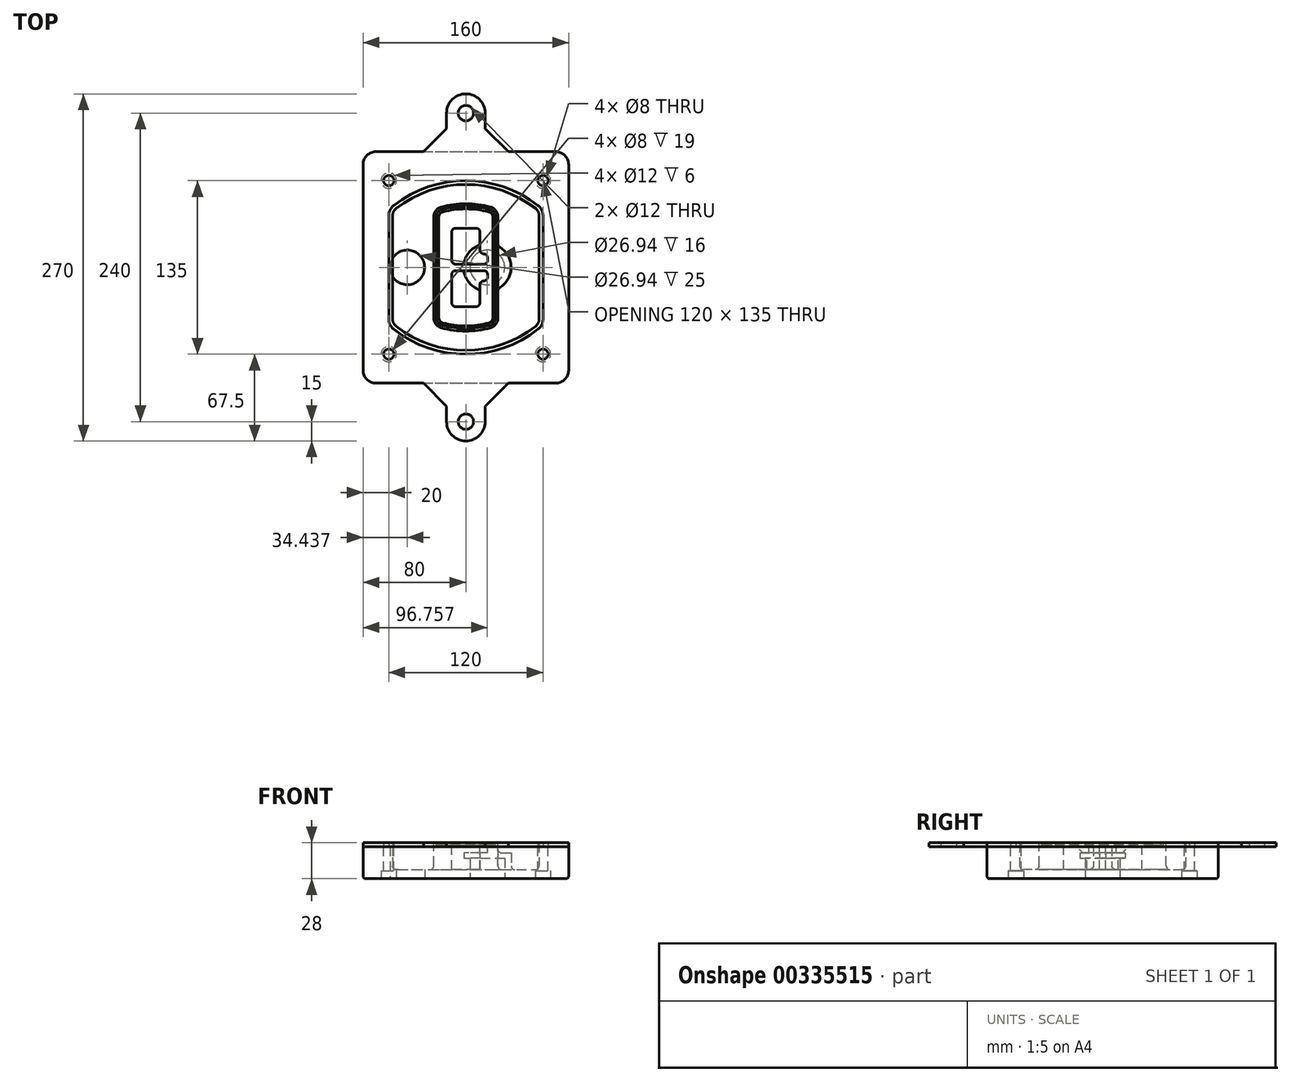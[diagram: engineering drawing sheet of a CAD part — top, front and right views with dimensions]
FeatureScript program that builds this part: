
annotation { "Feature Type Name" : "Feature", "Feature Type Description" : "" }
export const myFeature = defineFeature(function(context is Context, id is Id, definition is map)
    precondition{}
    {
        {
            var Q0;
            Q0=qCreatedBy(makeId("Top.planeOp"),FACE);
            var sketch = newSketch(context, id + "F0", { "sketchPlane" : qUnion([Q0])});
            skPoint(sketch, "E0.rect.middle", {"position": v(0, 0) * mm});
            skLineSegment(sketch, "E1.bottom", {"start": v(-70, -90) * mm, "end": v(70, -90) * mm});
            skLineSegment(sketch, "E1.top", {"start": v(-70, 90) * mm, "end": v(70, 90) * mm});
            skLineSegment(sketch, "E1.left", {"start": v(-80, -80) * mm, "end": v(-80, 80) * mm});
            skLineSegment(sketch, "E1.right", {"start": v(80, -80) * mm, "end": v(80, 80) * mm});
            skLineSegment(sketch, "E2", {"start": v(-80, 90) * mm, "end": v(80, -90) * mm, "construction": true});
            skLineSegment(sketch, "E3", {"start": v(80, 90) * mm, "end": v(-80, -90) * mm, "construction": true});
            skCircle(sketch, "E4", {"center": v(-60, 67.5) * mm, "radius": 4 * mm});
            skCircle(sketch, "E5", {"center": v(60, 67.5) * mm, "radius": 4 * mm});
            skCircle(sketch, "E6", {"center": v(60, -67.5) * mm, "radius": 4 * mm});
            skCircle(sketch, "E7", {"center": v(-60, -67.5) * mm, "radius": 4 * mm});
            skLineSegment(sketch, "E8", {"start": v(-60, 67.5) * mm, "end": v(60, 67.5) * mm, "construction": true});
            skLineSegment(sketch, "E9", {"start": v(60, 67.5) * mm, "end": v(60, -67.5) * mm, "construction": true});
            skLineSegment(sketch, "E10", {"start": v(60, -67.5) * mm, "end": v(-60, -67.5) * mm, "construction": true});
            skLineSegment(sketch, "E11", {"start": v(-60, -67.5) * mm, "end": v(-60, 67.5) * mm, "construction": true});
            skLineSegment(sketch, "E12", {"start": v(-60, 40.3) * mm, "end": v(-60, -40.3) * mm});
            skLineSegment(sketch, "E13", {"start": v(60, 40.3) * mm, "end": v(60, -40.3) * mm});
            skArc(sketch, "E14", {"start": v(56.15, 48.18) * mm, "mid": v(0, 67.5) * mm, "end": v(-56.15, 48.18) * mm});
            skArc(sketch, "E15", {"start": v(-56.15, -48.18) * mm, "mid": v(0, -67.5) * mm, "end": v(56.15, -48.18) * mm});
            skLineSegment(sketch, "E16", {"start": v(-60, 0) * mm, "end": v(60, 0) * mm, "construction": true});
            skPoint(sketch, "E17.visualSharp", {"position": v(-60, -45) * mm});
            skArc(sketch, "E17.filletArc", {"start": v(-60, -40.3) * mm, "mid": v(-58.99, -44.68) * mm, "end": v(-56.15, -48.18) * mm});
            skPoint(sketch, "E18.visualSharp", {"position": v(-60, 45) * mm});
            skArc(sketch, "E18.filletArc", {"start": v(-56.15, 48.18) * mm, "mid": v(-58.99, 44.68) * mm, "end": v(-60, 40.3) * mm});
            skPoint(sketch, "E19.visualSharp", {"position": v(60, 45) * mm});
            skArc(sketch, "E19.filletArc", {"start": v(60, 40.3) * mm, "mid": v(58.99, 44.68) * mm, "end": v(56.15, 48.18) * mm});
            skPoint(sketch, "E20.visualSharp", {"position": v(60, -45) * mm});
            skArc(sketch, "E20.filletArc", {"start": v(56.15, -48.18) * mm, "mid": v(58.99, -44.68) * mm, "end": v(60, -40.3) * mm});
            skPoint(sketch, "E21.visualSharp", {"position": v(-80, 90) * mm});
            skArc(sketch, "E21.filletArc", {"start": v(-70, 90) * mm, "mid": v(-77.07, 87.07) * mm, "end": v(-80, 80) * mm});
            skPoint(sketch, "E22.visualSharp", {"position": v(80, 90) * mm});
            skArc(sketch, "E22.filletArc", {"start": v(80, 80) * mm, "mid": v(77.07, 87.07) * mm, "end": v(70, 90) * mm});
            skPoint(sketch, "E23.visualSharp", {"position": v(80, -90) * mm});
            skArc(sketch, "E23.filletArc", {"start": v(70, -90) * mm, "mid": v(77.07, -87.07) * mm, "end": v(80, -80) * mm});
            skPoint(sketch, "E24.visualSharp", {"position": v(-80, -90) * mm});
            skArc(sketch, "E24.filletArc", {"start": v(-80, -80) * mm, "mid": v(-77.07, -87.07) * mm, "end": v(-70, -90) * mm});
            skArc(sketch, "E25.0", {"start": v(57, 40.3) * mm, "mid": v(56.3, 43.36) * mm, "end": v(54.3, 45.81) * mm});
            skLineSegment(sketch, "E25.1", {"start": v(57, 40.3) * mm, "end": v(57, -40.3) * mm});
            skArc(sketch, "E25.2", {"start": v(54.3, -45.81) * mm, "mid": v(56.3, -43.36) * mm, "end": v(57, -40.3) * mm});
            skArc(sketch, "E25.3", {"start": v(-54.3, -45.81) * mm, "mid": v(0, -64.5) * mm, "end": v(54.3, -45.81) * mm});
            skArc(sketch, "E25.4", {"start": v(-57, -40.3) * mm, "mid": v(-56.3, -43.36) * mm, "end": v(-54.3, -45.81) * mm});
            skArc(sketch, "E25.5", {"start": v(54.3, 45.81) * mm, "mid": v(0, 64.5) * mm, "end": v(-54.3, 45.81) * mm});
            skLineSegment(sketch, "E25.6", {"start": v(-57, 40.3) * mm, "end": v(-57, -40.3) * mm});
            skArc(sketch, "E25.7", {"start": v(-54.3, 45.81) * mm, "mid": v(-56.3, 43.36) * mm, "end": v(-57, 40.3) * mm});
            skArc(sketch, "E26.0", {"start": v(-58.62, 51.33) * mm, "mid": v(-62.58, 46.43) * mm, "end": v(-64, 40.3) * mm});
            skArc(sketch, "E26.1", {"start": v(58.62, 51.33) * mm, "mid": v(0, 71.5) * mm, "end": v(-58.62, 51.33) * mm});
            skArc(sketch, "E26.2", {"start": v(64, 40.3) * mm, "mid": v(62.58, 46.43) * mm, "end": v(58.62, 51.33) * mm});
            skLineSegment(sketch, "E26.3", {"start": v(64, 40.3) * mm, "end": v(64, -40.3) * mm});
            skArc(sketch, "E26.4", {"start": v(58.62, -51.33) * mm, "mid": v(62.58, -46.43) * mm, "end": v(64, -40.3) * mm});
            skLineSegment(sketch, "E26.5", {"start": v(-64, 40.3) * mm, "end": v(-64, -40.3) * mm});
            skArc(sketch, "E26.6", {"start": v(-58.62, -51.33) * mm, "mid": v(0, -71.5) * mm, "end": v(58.62, -51.33) * mm});
            skArc(sketch, "E26.7", {"start": v(-64, -40.3) * mm, "mid": v(-62.58, -46.43) * mm, "end": v(-58.62, -51.33) * mm});
            skSolve(sketch);
        }
        {
            var Q0;
            Q0=makeQuery(id+"F0.imprint","IMPRINT",FACE,{"disambiguationData":[TD([[makeQuery(id+"F0.imprint","IMPRINT",EDGE,{"derivedFrom":sQuery(id+"F0.wireOp",EDGE,"E1.bottom")}),1.0]])]});
            var Q1;
            Q1=makeQuery(id+"F0.imprint","IMPRINT",FACE,{"disambiguationData":[TD([[makeQuery(id+"F0.imprint","IMPRINT",EDGE,{"derivedFrom":sQuery(id+"F0.wireOp",EDGE,"E12")}),1.0]])]});
            var Q2;
            Q2=makeQuery(id+"F0.imprint","IMPRINT",FACE,{"disambiguationData":[TD([[makeQuery(id+"F0.imprint","IMPRINT",EDGE,{"derivedFrom":sQuery(id+"F0.wireOp",EDGE,"E25.0")}),1.0]])]});
            var Q3;
            Q3=makeQuery(id+"F0.imprint","IMPRINT",FACE,{"disambiguationData":[TD([[makeQuery(id+"F0.imprint","IMPRINT",EDGE,{"derivedFrom":sQuery(id+"F0.wireOp",EDGE,"E12")}),-1.0]])]});
            extrude(context, id + "F1", {"entities" : qUnion([Q0, Q1, Q2, Q3]), "oppositeDirection" : true, "depth" : 25 * mm});
        }
        {
            var Q0;
            Q0=makeQuery(id+"F0.imprint","IMPRINT",FACE,{"disambiguationData":[TD([[makeQuery(id+"F0.imprint","IMPRINT",EDGE,{"derivedFrom":sQuery(id+"F0.wireOp",EDGE,"E12")}),1.0]])]});
            extrude(context, id + "F2", {"entities" : qUnion([Q0]), "operationType" : NewBodyOperationType.ADD, "depth" : 3 * mm});
        }
        {
            var Q0;
            Q0=makeQuery(id+"F0.imprint","IMPRINT",FACE,{"disambiguationData":[TD([[makeQuery(id+"F0.imprint","IMPRINT",EDGE,{"derivedFrom":sQuery(id+"F0.wireOp",EDGE,"E25.0")}),1.0]])]});
            extrude(context, id + "F3", {"entities" : qUnion([Q0]), "operationType" : NewBodyOperationType.REMOVE, "oppositeDirection" : true, "depth" : 18 * mm});
        }
        {
            var Q0;
            Q0=makeQuery(id+"F2.opExtrude","CAP_FACE",FACE,{"disambiguationData":[OSD([sQuery(id+"F0.wireOp",EDGE,"E12"),sQuery(id+"F0.wireOp",EDGE,"E13"),sQuery(id+"F0.wireOp",EDGE,"E14"),sQuery(id+"F0.wireOp",EDGE,"E15"),sQuery(id+"F0.wireOp",EDGE,"E17.filletArc"),sQuery(id+"F0.wireOp",EDGE,"E18.filletArc"),sQuery(id+"F0.wireOp",EDGE,"E19.filletArc"),sQuery(id+"F0.wireOp",EDGE,"E20.filletArc"),sQuery(id+"F0.wireOp",EDGE,"E25.0"),sQuery(id+"F0.wireOp",EDGE,"E25.1"),sQuery(id+"F0.wireOp",EDGE,"E25.2"),sQuery(id+"F0.wireOp",EDGE,"E25.3"),sQuery(id+"F0.wireOp",EDGE,"E25.4"),sQuery(id+"F0.wireOp",EDGE,"E25.5"),sQuery(id+"F0.wireOp",EDGE,"E25.6"),sQuery(id+"F0.wireOp",EDGE,"E25.7")])],"isStart":false});
            var sketch = newSketch(context, id + "F4", { "sketchPlane" : qUnion([Q0])});
            skArc(sketch, "E27.0", {"start": v(-19.08, -46.97) * mm, "mid": v(0, -49.5) * mm, "end": v(19.08, -46.97) * mm});
            skArc(sketch, "E28.0", {"start": v(19.08, 46.97) * mm, "mid": v(0, 49.5) * mm, "end": v(-19.08, 46.97) * mm});
            skLineSegment(sketch, "E29", {"start": v(-25, 39.25) * mm, "end": v(-25, -39.25) * mm});
            skLineSegment(sketch, "E30", {"start": v(25, 39.25) * mm, "end": v(25, -39.25) * mm});
            skLineSegment(sketch, "E31", {"start": v(-25, 45.1) * mm, "end": v(25, 45.1) * mm, "construction": true});
            skLineSegment(sketch, "E32", {"start": v(-25, -45.1) * mm, "end": v(25, -45.1) * mm, "construction": true});
            skPoint(sketch, "E33.visualSharp", {"position": v(-25, 45.1) * mm});
            skArc(sketch, "E33.filletArc", {"start": v(-19.08, 46.97) * mm, "mid": v(-23.35, 44.11) * mm, "end": v(-25, 39.25) * mm});
            skPoint(sketch, "E34.visualSharp", {"position": v(25, 45.1) * mm});
            skArc(sketch, "E34.filletArc", {"start": v(25, 39.25) * mm, "mid": v(23.35, 44.11) * mm, "end": v(19.08, 46.97) * mm});
            skPoint(sketch, "E35.visualSharp", {"position": v(25, -45.1) * mm});
            skArc(sketch, "E35.filletArc", {"start": v(19.08, -46.97) * mm, "mid": v(23.35, -44.11) * mm, "end": v(25, -39.25) * mm});
            skPoint(sketch, "E36.visualSharp", {"position": v(-25, -45.1) * mm});
            skArc(sketch, "E36.filletArc", {"start": v(-25, -39.25) * mm, "mid": v(-23.35, -44.11) * mm, "end": v(-19.08, -46.97) * mm});
            skArc(sketch, "E37.0", {"start": v(54.3, 45.81) * mm, "mid": v(0, 64.5) * mm, "end": v(-54.3, 45.81) * mm});
            skArc(sketch, "E37.1", {"start": v(-54.3, 45.81) * mm, "mid": v(-56.3, 43.36) * mm, "end": v(-57, 40.3) * mm});
            skLineSegment(sketch, "E37.2", {"start": v(-57, 40.3) * mm, "end": v(-57, -40.3) * mm});
            skArc(sketch, "E37.3", {"start": v(-57, -40.3) * mm, "mid": v(-56.3, -43.36) * mm, "end": v(-54.3, -45.81) * mm});
            skArc(sketch, "E37.4", {"start": v(-54.3, -45.81) * mm, "mid": v(0, -64.5) * mm, "end": v(54.3, -45.81) * mm});
            skArc(sketch, "E37.5", {"start": v(54.3, -45.81) * mm, "mid": v(56.3, -43.36) * mm, "end": v(57, -40.3) * mm});
            skLineSegment(sketch, "E37.6", {"start": v(57, 40.3) * mm, "end": v(57, -40.3) * mm});
            skArc(sketch, "E37.7", {"start": v(57, 40.3) * mm, "mid": v(56.3, 43.36) * mm, "end": v(54.3, 45.81) * mm});
            skLineSegment(sketch, "E38.0", {"start": v(23, 39.25) * mm, "end": v(23, -39.25) * mm});
            skArc(sketch, "E38.1", {"start": v(18.56, -45.04) * mm, "mid": v(21.76, -42.9) * mm, "end": v(23, -39.25) * mm});
            skArc(sketch, "E38.2", {"start": v(-18.56, -45.04) * mm, "mid": v(0, -47.5) * mm, "end": v(18.56, -45.04) * mm});
            skArc(sketch, "E38.3", {"start": v(-23, -39.25) * mm, "mid": v(-21.76, -42.9) * mm, "end": v(-18.56, -45.04) * mm});
            skLineSegment(sketch, "E38.4", {"start": v(-23, 39.25) * mm, "end": v(-23, -39.25) * mm});
            skArc(sketch, "E38.5", {"start": v(23, 39.25) * mm, "mid": v(21.76, 42.9) * mm, "end": v(18.56, 45.04) * mm});
            skArc(sketch, "E38.6", {"start": v(-18.56, 45.04) * mm, "mid": v(-21.76, 42.9) * mm, "end": v(-23, 39.25) * mm});
            skArc(sketch, "E38.7", {"start": v(18.56, 45.04) * mm, "mid": v(0, 47.5) * mm, "end": v(-18.56, 45.04) * mm});
            skArc(sketch, "E39.0", {"start": v(21, 39.25) * mm, "mid": v(20.18, 41.68) * mm, "end": v(18.04, 43.1) * mm});
            skLineSegment(sketch, "E39.1", {"start": v(21, 39.25) * mm, "end": v(21, -39.25) * mm});
            skArc(sketch, "E39.2", {"start": v(18.04, -43.1) * mm, "mid": v(20.18, -41.68) * mm, "end": v(21, -39.25) * mm});
            skArc(sketch, "E39.3", {"start": v(-18.04, -43.1) * mm, "mid": v(0, -45.5) * mm, "end": v(18.04, -43.1) * mm});
            skArc(sketch, "E39.4", {"start": v(-21, -39.25) * mm, "mid": v(-20.18, -41.68) * mm, "end": v(-18.04, -43.1) * mm});
            skArc(sketch, "E39.5", {"start": v(18.04, 43.1) * mm, "mid": v(0, 45.5) * mm, "end": v(-18.04, 43.1) * mm});
            skLineSegment(sketch, "E39.6", {"start": v(-21, 39.25) * mm, "end": v(-21, -39.25) * mm});
            skArc(sketch, "E39.7", {"start": v(-18.04, 43.1) * mm, "mid": v(-20.18, 41.68) * mm, "end": v(-21, 39.25) * mm});
            skLineSegment(sketch, "E40", {"start": v(-25, 0) * mm, "end": v(25, 0) * mm, "construction": true});
            skLineSegment(sketch, "E41", {"start": v(-11, 5.5) * mm, "end": v(-11, 27.5) * mm});
            skLineSegment(sketch, "E42", {"start": v(-8, 30.5) * mm, "end": v(8, 30.5) * mm});
            skLineSegment(sketch, "E43", {"start": v(11, 27.5) * mm, "end": v(11, 13.5) * mm});
            skLineSegment(sketch, "E44", {"start": v(14, 10.5) * mm, "end": v(14, 10.5) * mm});
            skLineSegment(sketch, "E45", {"start": v(17, 7.5) * mm, "end": v(17, 5.5) * mm});
            skLineSegment(sketch, "E46", {"start": v(14, 2.5) * mm, "end": v(-8, 2.5) * mm});
            skPoint(sketch, "E47.visualSharp", {"position": v(-11, 30.5) * mm});
            skArc(sketch, "E47.filletArc", {"start": v(-8, 30.5) * mm, "mid": v(-10.12, 29.62) * mm, "end": v(-11, 27.5) * mm});
            skPoint(sketch, "E48.visualSharp", {"position": v(11, 30.5) * mm});
            skArc(sketch, "E48.filletArc", {"start": v(11, 27.5) * mm, "mid": v(10.12, 29.62) * mm, "end": v(8, 30.5) * mm});
            skPoint(sketch, "E49.visualSharp", {"position": v(11, 10.5) * mm});
            skArc(sketch, "E49.filletArc", {"start": v(11, 13.5) * mm, "mid": v(11.88, 11.38) * mm, "end": v(14, 10.5) * mm});
            skPoint(sketch, "E50.visualSharp", {"position": v(17, 10.5) * mm});
            skArc(sketch, "E50.filletArc", {"start": v(17, 7.5) * mm, "mid": v(16.12, 9.62) * mm, "end": v(14, 10.5) * mm});
            skPoint(sketch, "E51.visualSharp", {"position": v(17, 2.5) * mm});
            skArc(sketch, "E51.filletArc", {"start": v(14, 2.5) * mm, "mid": v(16.12, 3.38) * mm, "end": v(17, 5.5) * mm});
            skPoint(sketch, "E52.visualSharp", {"position": v(-11, 2.5) * mm});
            skArc(sketch, "E52.filletArc", {"start": v(-11, 5.5) * mm, "mid": v(-10.12, 3.38) * mm, "end": v(-8, 2.5) * mm});
            skLineSegment(sketch, "E53.0.MirrorCS", {"start": v(14, -2.5) * mm, "end": v(-8, -2.5) * mm});
            skArc(sketch, "E54.0.MirrorCS", {"start": v(-11, -5.5) * mm, "mid": v(-10.12, -3.38) * mm, "end": v(-8, -2.5) * mm});
            skLineSegment(sketch, "E55.0.MirrorCS", {"start": v(-11, -5.5) * mm, "end": v(-11, -27.5) * mm});
            skArc(sketch, "E56.0.MirrorCS", {"start": v(-8, -30.5) * mm, "mid": v(-10.12, -29.62) * mm, "end": v(-11, -27.5) * mm});
            skLineSegment(sketch, "E57.0.MirrorCS", {"start": v(-8, -30.5) * mm, "end": v(8, -30.5) * mm});
            skArc(sketch, "E58.0.MirrorCS", {"start": v(11, -27.5) * mm, "mid": v(10.12, -29.62) * mm, "end": v(8, -30.5) * mm});
            skLineSegment(sketch, "E59.0.MirrorCS", {"start": v(11, -27.5) * mm, "end": v(11, -13.5) * mm});
            skArc(sketch, "E60.0.MirrorCS", {"start": v(11, -13.5) * mm, "mid": v(11.88, -11.38) * mm, "end": v(14, -10.5) * mm});
            skArc(sketch, "E61.0.MirrorCS", {"start": v(17, -7.5) * mm, "mid": v(16.12, -9.62) * mm, "end": v(14, -10.5) * mm});
            skLineSegment(sketch, "E62.0.MirrorCS", {"start": v(17, -7.5) * mm, "end": v(17, -5.5) * mm});
            skArc(sketch, "E63.0.MirrorCS", {"start": v(14, -2.5) * mm, "mid": v(16.12, -3.38) * mm, "end": v(17, -5.5) * mm});
            skSolve(sketch);
        }
        {
            var Q0;
            Q0=makeQuery(id+"F4.imprint","IMPRINT",FACE,{"disambiguationData":[TD([[makeQuery(id+"F4.imprint","IMPRINT",EDGE,{"derivedFrom":sQuery(id+"F4.wireOp",EDGE,"E27.0")}),1.0]])]});
            var Q1;
            Q1=makeQuery(id+"F4.imprint","IMPRINT",FACE,{"disambiguationData":[TD([[makeQuery(id+"F4.imprint","IMPRINT",EDGE,{"derivedFrom":sQuery(id+"F4.wireOp",EDGE,"E38.0")}),-1.0]])]});
            var Q2;
            Q2=makeQuery(id+"F4.imprint","IMPRINT",FACE,{"disambiguationData":[TD([[makeQuery(id+"F4.imprint","IMPRINT",EDGE,{"derivedFrom":sQuery(id+"F4.wireOp",EDGE,"E39.0")}),1.0]])]});
            extrude(context, id + "F5", {"entities" : qUnion([Q0, Q1, Q2]), "operationType" : NewBodyOperationType.ADD, "endBound" : BoundingType.UP_TO_NEXT, "oppositeDirection" : true, "depth" : 25 * mm});
        }
        {
            var Q0;
            Q0=makeQuery(id+"F4.imprint","IMPRINT",FACE,{"disambiguationData":[TD([[makeQuery(id+"F4.imprint","IMPRINT",EDGE,{"derivedFrom":sQuery(id+"F4.wireOp",EDGE,"E38.0")}),-1.0]])]});
            extrude(context, id + "F6", {"entities" : qUnion([Q0]), "operationType" : NewBodyOperationType.REMOVE, "oppositeDirection" : true, "depth" : 2 * mm});
        }
        {
            var Q0;
            Q0=makeQuery(id+"F1.opExtrude","CAP_FACE",FACE,{"disambiguationData":[OSD([sQuery(id+"F0.wireOp",EDGE,"E1.bottom"),sQuery(id+"F0.wireOp",EDGE,"E1.top"),sQuery(id+"F0.wireOp",EDGE,"E1.left"),sQuery(id+"F0.wireOp",EDGE,"E1.right"),sQuery(id+"F0.wireOp",EDGE,"E4"),sQuery(id+"F0.wireOp",EDGE,"E5"),sQuery(id+"F0.wireOp",EDGE,"E6"),sQuery(id+"F0.wireOp",EDGE,"E7"),sQuery(id+"F0.wireOp",EDGE,"E21.filletArc"),sQuery(id+"F0.wireOp",EDGE,"E22.filletArc"),sQuery(id+"F0.wireOp",EDGE,"E23.filletArc"),sQuery(id+"F0.wireOp",EDGE,"E24.filletArc")])],"isStart":false});
            var sketch = newSketch(context, id + "F7", { "sketchPlane" : qUnion([Q0])});
            skCircle(sketch, "E64", {"center": v(16.76, 0) * mm, "radius": 13.47 * mm});
            skCircle(sketch, "E65", {"center": v(-45.56, 0) * mm, "radius": 13.47 * mm});
            skLineSegment(sketch, "E66", {"start": v(80, 0) * mm, "end": v(-80, 0) * mm});
            skCircle(sketch, "E67", {"center": v(16.76, 0) * mm, "radius": 18.47 * mm});
            skCircle(sketch, "E68", {"center": v(60, -67.5) * mm, "radius": 6 * mm});
            skCircle(sketch, "E69", {"center": v(-60, -67.5) * mm, "radius": 6 * mm});
            skCircle(sketch, "E70", {"center": v(-60, 67.5) * mm, "radius": 6 * mm});
            skCircle(sketch, "E71", {"center": v(60, 67.5) * mm, "radius": 6 * mm});
            skSolve(sketch);
        }
        {
            var Q0;
            {var subQ1=sQuery(id+"F7.wireOp",EDGE,"E66");var subQ4=sQuery(id+"F7.wireOp",EDGE,"E64");var subQ6=makeQuery(id+"F7.imprint","INTERSECT",VERTEX,{"disambiguationData":[OD(0.0)],"derivedFrom":[subQ4,subQ1]});Q0=makeQuery(id+"F7.imprint","IMPRINT",FACE,{"disambiguationData":[TD([[makeQuery(id+"F7.imprint","IMPRINT",EDGE,{"disambiguationData":[TD([[subQ6,-1.0]])],"derivedFrom":subQ4}),-1.0]])]});}
            var Q1;
            {var subQ0=sQuery(id+"F7.wireOp",EDGE,"E66");var subQ1=sQuery(id+"F7.wireOp",EDGE,"E64");var subQ3=makeQuery(id+"F7.imprint","INTERSECT",VERTEX,{"disambiguationData":[OD(0.0)],"derivedFrom":[subQ1,subQ0]});Q1=makeQuery(id+"F7.imprint","IMPRINT",FACE,{"disambiguationData":[TD([[makeQuery(id+"F7.imprint","IMPRINT",EDGE,{"disambiguationData":[TD([[subQ3,-1.0]])],"derivedFrom":subQ1}),1.0]])]});}
            var Q2;
            {var subQ0=sQuery(id+"F7.wireOp",EDGE,"E66");var subQ1=sQuery(id+"F7.wireOp",EDGE,"E64");var subQ3=makeQuery(id+"F7.imprint","INTERSECT",VERTEX,{"disambiguationData":[OD(0.0)],"derivedFrom":[subQ1,subQ0]});Q2=makeQuery(id+"F7.imprint","IMPRINT",FACE,{"disambiguationData":[TD([[makeQuery(id+"F7.imprint","IMPRINT",EDGE,{"disambiguationData":[TD([[subQ3,1.0]])],"derivedFrom":subQ1}),1.0]])]});}
            var Q3;
            {var subQ1=sQuery(id+"F7.wireOp",EDGE,"E66");var subQ4=sQuery(id+"F7.wireOp",EDGE,"E64");var subQ6=makeQuery(id+"F7.imprint","INTERSECT",VERTEX,{"disambiguationData":[OD(0.0)],"derivedFrom":[subQ4,subQ1]});Q3=makeQuery(id+"F7.imprint","IMPRINT",FACE,{"disambiguationData":[TD([[makeQuery(id+"F7.imprint","IMPRINT",EDGE,{"disambiguationData":[TD([[subQ6,1.0]])],"derivedFrom":subQ4}),-1.0]])]});}
            extrude(context, id + "F8", {"entities" : qUnion([Q0, Q1, Q2, Q3]), "operationType" : NewBodyOperationType.ADD, "oppositeDirection" : true, "depth" : 20 * mm});
        }
        {
            var Q0;
            {var subQ0=sQuery(id+"F7.wireOp",EDGE,"E66");var subQ1=sQuery(id+"F7.wireOp",EDGE,"E64");var subQ3=makeQuery(id+"F7.imprint","INTERSECT",VERTEX,{"disambiguationData":[OD(0.0)],"derivedFrom":[subQ1,subQ0]});Q0=makeQuery(id+"F7.imprint","IMPRINT",FACE,{"disambiguationData":[TD([[makeQuery(id+"F7.imprint","IMPRINT",EDGE,{"disambiguationData":[TD([[subQ3,-1.0]])],"derivedFrom":subQ1}),1.0]])]});}
            var Q1;
            {var subQ0=sQuery(id+"F7.wireOp",EDGE,"E66");var subQ1=sQuery(id+"F7.wireOp",EDGE,"E64");var subQ3=makeQuery(id+"F7.imprint","INTERSECT",VERTEX,{"disambiguationData":[OD(0.0)],"derivedFrom":[subQ1,subQ0]});Q1=makeQuery(id+"F7.imprint","IMPRINT",FACE,{"disambiguationData":[TD([[makeQuery(id+"F7.imprint","IMPRINT",EDGE,{"disambiguationData":[TD([[subQ3,1.0]])],"derivedFrom":subQ1}),1.0]])]});}
            extrude(context, id + "F9", {"entities" : qUnion([Q0, Q1]), "operationType" : NewBodyOperationType.REMOVE, "oppositeDirection" : true, "depth" : 16 * mm});
        }
        {
            var Q0;
            {var subQ0=sQuery(id+"F7.wireOp",EDGE,"E66");var subQ1=sQuery(id+"F7.wireOp",EDGE,"E65");var subQ3=makeQuery(id+"F7.imprint","INTERSECT",VERTEX,{"disambiguationData":[OD(0.0)],"derivedFrom":[subQ1,subQ0]});Q0=makeQuery(id+"F7.imprint","IMPRINT",FACE,{"disambiguationData":[TD([[makeQuery(id+"F7.imprint","IMPRINT",EDGE,{"disambiguationData":[TD([[subQ3,-1.0]])],"derivedFrom":subQ1}),1.0]])]});}
            var Q1;
            {var subQ0=sQuery(id+"F7.wireOp",EDGE,"E66");var subQ1=sQuery(id+"F7.wireOp",EDGE,"E65");var subQ3=makeQuery(id+"F7.imprint","INTERSECT",VERTEX,{"disambiguationData":[OD(0.0)],"derivedFrom":[subQ1,subQ0]});Q1=makeQuery(id+"F7.imprint","IMPRINT",FACE,{"disambiguationData":[TD([[makeQuery(id+"F7.imprint","IMPRINT",EDGE,{"disambiguationData":[TD([[subQ3,1.0]])],"derivedFrom":subQ1}),1.0]])]});}
            extrude(context, id + "F10", {"entities" : qUnion([Q0, Q1]), "operationType" : NewBodyOperationType.REMOVE, "oppositeDirection" : true, "depth" : 25 * mm});
        }
        {
            var Q0;
            Q0=makeQuery(id+"F7.imprint","IMPRINT",FACE,{"disambiguationData":[TD([[makeQuery(id+"F7.imprint","IMPRINT",EDGE,{"derivedFrom":sQuery(id+"F7.wireOp",EDGE,"E68")}),1.0]])]});
            var Q1;
            Q1=makeQuery(id+"F7.imprint","IMPRINT",FACE,{"disambiguationData":[TD([[makeQuery(id+"F7.imprint","IMPRINT",EDGE,{"derivedFrom":makeQuery(id+"F1.opExtrude","CAP_EDGE",EDGE,{"disambiguationData":[OSD([sQuery(id+"F0.wireOp",EDGE,"E5")])],"isStart":false})}),-1.0]])]});
            var Q2;
            Q2=makeQuery(id+"F7.imprint","IMPRINT",FACE,{"disambiguationData":[TD([[makeQuery(id+"F7.imprint","IMPRINT",EDGE,{"derivedFrom":sQuery(id+"F7.wireOp",EDGE,"E69")}),1.0]])]});
            var Q3;
            Q3=makeQuery(id+"F7.imprint","IMPRINT",FACE,{"disambiguationData":[TD([[makeQuery(id+"F7.imprint","IMPRINT",EDGE,{"derivedFrom":makeQuery(id+"F1.opExtrude","CAP_EDGE",EDGE,{"disambiguationData":[OSD([sQuery(id+"F0.wireOp",EDGE,"E4")])],"isStart":false})}),-1.0]])]});
            var Q4;
            Q4=makeQuery(id+"F7.imprint","IMPRINT",FACE,{"disambiguationData":[TD([[makeQuery(id+"F7.imprint","IMPRINT",EDGE,{"derivedFrom":sQuery(id+"F7.wireOp",EDGE,"E70")}),1.0]])]});
            var Q5;
            Q5=makeQuery(id+"F7.imprint","IMPRINT",FACE,{"disambiguationData":[TD([[makeQuery(id+"F7.imprint","IMPRINT",EDGE,{"derivedFrom":makeQuery(id+"F1.opExtrude","CAP_EDGE",EDGE,{"disambiguationData":[OSD([sQuery(id+"F0.wireOp",EDGE,"E7")])],"isStart":false})}),-1.0]])]});
            var Q6;
            Q6=makeQuery(id+"F7.imprint","IMPRINT",FACE,{"disambiguationData":[TD([[makeQuery(id+"F7.imprint","IMPRINT",EDGE,{"derivedFrom":sQuery(id+"F7.wireOp",EDGE,"E71")}),1.0]])]});
            var Q7;
            Q7=makeQuery(id+"F7.imprint","IMPRINT",FACE,{"disambiguationData":[TD([[makeQuery(id+"F7.imprint","IMPRINT",EDGE,{"derivedFrom":makeQuery(id+"F1.opExtrude","CAP_EDGE",EDGE,{"disambiguationData":[OSD([sQuery(id+"F0.wireOp",EDGE,"E6")])],"isStart":false})}),-1.0]])]});
            extrude(context, id + "F11", {"entities" : qUnion([Q0, Q1, Q2, Q3, Q4, Q5, Q6, Q7]), "operationType" : NewBodyOperationType.REMOVE, "oppositeDirection" : true, "depth" : 6 * mm});
        }
        {
            var Q0;
            Q0=makeQuery(id+"F9.boolean.opBoolean","COPY",FACE,{"derivedFrom":makeQuery(id+"F9.opExtrude","CAP_FACE",FACE,{"disambiguationData":[OSD([sQuery(id+"F7.wireOp",EDGE,"E64")])],"isStart":false})});
            var sketch = newSketch(context, id + "F12", { "sketchPlane" : qUnion([Q0])});
            skArc(sketch, "E72.0", {"start": v(11, 17.55) * mm, "mid": v(2.57, 11.82) * mm, "end": v(-1.54, 2.5) * mm});
            skArc(sketch, "E72.1", {"start": v(-1.54, -2.5) * mm, "mid": v(2.57, -11.82) * mm, "end": v(11, -17.55) * mm});
            skLineSegment(sketch, "E73", {"start": v(-1.54, -2.5) * mm, "end": v(14, -2.5) * mm});
            skLineSegment(sketch, "E74.0", {"start": v(14, 2.5) * mm, "end": v(-1.54, 2.5) * mm});
            skArc(sketch, "E74.1", {"start": v(14, 2.5) * mm, "mid": v(16.12, 3.38) * mm, "end": v(17, 5.5) * mm});
            skLineSegment(sketch, "E74.2", {"start": v(17, 7.5) * mm, "end": v(17, 5.5) * mm});
            skArc(sketch, "E74.3", {"start": v(17, 7.5) * mm, "mid": v(16.12, 9.62) * mm, "end": v(14, 10.5) * mm});
            skArc(sketch, "E74.4", {"start": v(11, 13.5) * mm, "mid": v(11.88, 11.38) * mm, "end": v(14, 10.5) * mm});
            skLineSegment(sketch, "E74.5", {"start": v(11, 17.55) * mm, "end": v(11, 13.5) * mm});
            skLineSegment(sketch, "E74.7", {"start": v(14, -2.5) * mm, "end": v(-1.54, -2.5) * mm});
            skArc(sketch, "E74.8", {"start": v(14, -2.5) * mm, "mid": v(16.12, -3.38) * mm, "end": v(17, -5.5) * mm});
            skLineSegment(sketch, "E74.9", {"start": v(17, -7.5) * mm, "end": v(17, -5.5) * mm});
            skArc(sketch, "E74.10", {"start": v(17, -7.5) * mm, "mid": v(16.12, -9.62) * mm, "end": v(14, -10.5) * mm});
            skArc(sketch, "E74.11", {"start": v(11, -13.5) * mm, "mid": v(11.88, -11.38) * mm, "end": v(14, -10.5) * mm});
            skLineSegment(sketch, "E74.12", {"start": v(11, -17.55) * mm, "end": v(11, -13.5) * mm});
            skPoint(sketch, "E75.orphan", {"position": v(11, -27.5) * mm});
            skPoint(sketch, "E76.orphan", {"position": v(-8, -2.5) * mm});
            skPoint(sketch, "E77.orphan", {"position": v(-8, 2.5) * mm});
            skPoint(sketch, "E78.orphan", {"position": v(11, 27.5) * mm});
            skSolve(sketch);
        }
        {
            var Q0;
            {var subQ7=sQuery(id+"F12.wireOp",EDGE,"E72.0");var subQ14=sQuery(id+"F12.wireOp",EDGE,"E72.1");var subQ16=sQuery(id+"F12.wireOp",EDGE,"E74.1");var subQ18=sQuery(id+"F12.wireOp",EDGE,"E74.8");Q0=qUnion([makeQuery(id+"F12.imprint","IMPRINT",FACE,{"disambiguationData":[TD([[makeQuery(id+"F12.imprint","IMPRINT",EDGE,{"derivedFrom":subQ7}),1.0]])]}),makeQuery(id+"F12.imprint","IMPRINT",FACE,{"disambiguationData":[TD([[makeQuery(id+"F12.imprint","IMPRINT",EDGE,{"derivedFrom":subQ14}),1.0]])]}),makeQuery(id+"F12.imprint","IMPRINT",FACE,{"disambiguationData":[TD([[makeQuery(id+"F12.imprint","IMPRINT",EDGE,{"derivedFrom":subQ16}),1.0]])]}),makeQuery(id+"F12.imprint","IMPRINT",FACE,{"disambiguationData":[TD([[makeQuery(id+"F12.imprint","IMPRINT",EDGE,{"derivedFrom":subQ18}),-1.0]])]})]);}
            var Q1;
            Q1=makeQuery(id+"F5.boolean.opBoolean","SPLIT",FACE,{"disambiguationData":[TD([makeQuery(id+"F5.opExtrude","SWEPT_FACE",FACE,{"disambiguationData":[OSD([sQuery(id+"F4.wireOp",EDGE,"E41")])]})])],"derivedFrom":makeQuery(id+"F3.boolean.opBoolean","COPY",FACE,{"derivedFrom":makeQuery(id+"F3.opExtrude","CAP_FACE",FACE,{"disambiguationData":[OSD([sQuery(id+"F0.wireOp",EDGE,"E25.0"),sQuery(id+"F0.wireOp",EDGE,"E25.1"),sQuery(id+"F0.wireOp",EDGE,"E25.2"),sQuery(id+"F0.wireOp",EDGE,"E25.3"),sQuery(id+"F0.wireOp",EDGE,"E25.4"),sQuery(id+"F0.wireOp",EDGE,"E25.5"),sQuery(id+"F0.wireOp",EDGE,"E25.6"),sQuery(id+"F0.wireOp",EDGE,"E25.7")])],"isStart":false})})});
            extrude(context, id + "F13", {"entities" : qUnion([Q0]), "operationType" : NewBodyOperationType.REMOVE, "endBound" : BoundingType.UP_TO_SURFACE, "endBoundEntityFace" : qUnion([Q1]), "depth" : 25 * mm});
        }
        {
            var Q0;
            Q0=makeQuery(id+"F3.boolean.opBoolean","COPY",EDGE,{"derivedFrom":makeQuery(id+"F3.opExtrude","CAP_EDGE",EDGE,{"disambiguationData":[OSD([sQuery(id+"F0.wireOp",EDGE,"E25.6")])],"isStart":false})});
            var Q1;
            Q1=makeQuery(id+"F8.boolean.opBoolean","INTERSECT",EDGE,{"derivedFrom":[makeQuery(id+"F5.opExtrude","SWEPT_FACE",FACE,{"disambiguationData":[OSD([sQuery(id+"F4.wireOp",EDGE,"E30")])]}),makeQuery(id+"F8.opExtrude","CAP_FACE",FACE,{"disambiguationData":[OSD([sQuery(id+"F7.wireOp",EDGE,"E67")])],"isStart":false})]});
            var Q2;
            Q2=makeQuery(id+"F8.boolean.opBoolean","INTERSECT",EDGE,{"disambiguationData":[OD(1.0)],"derivedFrom":[makeQuery(id+"F5.opExtrude","SWEPT_FACE",FACE,{"disambiguationData":[OSD([sQuery(id+"F4.wireOp",EDGE,"E30")])]}),makeQuery(id+"F8.opExtrude","SWEPT_FACE",FACE,{"disambiguationData":[OSD([sQuery(id+"F7.wireOp",EDGE,"E67")])]})]});
            var Q3;
            {var subQ0=sQuery(id+"F4.wireOp",EDGE,"E30");Q3=makeQuery(id+"F8.boolean.opBoolean","SPLIT",EDGE,{"disambiguationData":[TD([makeQuery(id+"F5.opExtrude","SWEPT_FACE",FACE,{"disambiguationData":[OSD([sQuery(id+"F4.wireOp",EDGE,"E35.filletArc")])]})])],"derivedFrom":makeQuery(id+"F5.opExtrude","CAP_EDGE",EDGE,{"disambiguationData":[OSD([subQ0])],"isStart":false})});}
            var Q4;
            {var subQ0=sQuery(id+"F0.wireOp",EDGE,"E25.7");var subQ1=sQuery(id+"F0.wireOp",EDGE,"E25.1");var subQ2=sQuery(id+"F0.wireOp",EDGE,"E25.6");var subQ3=sQuery(id+"F0.wireOp",EDGE,"E25.5");var subQ4=sQuery(id+"F0.wireOp",EDGE,"E25.4");var subQ5=sQuery(id+"F0.wireOp",EDGE,"E25.0");var subQ6=sQuery(id+"F0.wireOp",EDGE,"E25.2");var subQ7=sQuery(id+"F0.wireOp",EDGE,"E25.3");Q4=makeQuery(id+"F8.boolean.opBoolean","INTERSECT",EDGE,{"derivedFrom":[makeQuery(id+"F5.boolean.opBoolean","SPLIT",FACE,{"disambiguationData":[TD([makeQuery(id+"F2.opExtrude","SWEPT_FACE",FACE,{"disambiguationData":[OSD([subQ5])]})])],"derivedFrom":makeQuery(id+"F3.boolean.opBoolean","COPY",FACE,{"derivedFrom":makeQuery(id+"F3.opExtrude","CAP_FACE",FACE,{"disambiguationData":[OSD([subQ5,subQ1,subQ6,subQ7,subQ4,subQ3,subQ2,subQ0])],"isStart":false})})}),makeQuery(id+"F8.opExtrude","SWEPT_FACE",FACE,{"disambiguationData":[OSD([sQuery(id+"F7.wireOp",EDGE,"E67")])]})]});}
            var Q5;
            Q5=makeQuery(id+"F8.boolean.opBoolean","INTERSECT",EDGE,{"disambiguationData":[OD(0.0)],"derivedFrom":[makeQuery(id+"F5.opExtrude","SWEPT_FACE",FACE,{"disambiguationData":[OSD([sQuery(id+"F4.wireOp",EDGE,"E30")])]}),makeQuery(id+"F8.opExtrude","SWEPT_FACE",FACE,{"disambiguationData":[OSD([sQuery(id+"F7.wireOp",EDGE,"E67")])]})]});
            fillet(context, id + "F14", {"entities" : qUnion([Q0, Q1, Q2, Q3, Q4, Q5]), "radius" : 3 * mm, "tangentPropagation" : true, "allowEdgeOverflow" : false});
        }
        {
            var Q0;
            Q0=makeQuery(id+"F1.opExtrude","CAP_EDGE",EDGE,{"disambiguationData":[OSD([sQuery(id+"F0.wireOp",EDGE,"E1.bottom")])],"isStart":false});
            fillet(context, id + "F15", {"entities" : qUnion([Q0]), "radius" : 2 * mm, "tangentPropagation" : true, "allowEdgeOverflow" : false});
        }
        {
            var Q0;
            {var subQ0=sQuery(id+"F0.wireOp",EDGE,"E21.filletArc");var subQ1=sQuery(id+"F0.wireOp",EDGE,"E7");var subQ2=sQuery(id+"F0.wireOp",EDGE,"E6");var subQ3=sQuery(id+"F0.wireOp",EDGE,"E5");var subQ4=sQuery(id+"F0.wireOp",EDGE,"E4");var subQ5=sQuery(id+"F0.wireOp",EDGE,"E22.filletArc");var subQ6=sQuery(id+"F0.wireOp",EDGE,"E1.bottom");var subQ7=sQuery(id+"F0.wireOp",EDGE,"E1.right");var subQ8=sQuery(id+"F0.wireOp",EDGE,"E1.top");var subQ9=sQuery(id+"F0.wireOp",EDGE,"E1.left");var subQ10=sQuery(id+"F0.wireOp",EDGE,"E23.filletArc");var subQ11=sQuery(id+"F0.wireOp",EDGE,"E24.filletArc");Q0=makeQuery(id+"F2.boolean.opBoolean","SPLIT",FACE,{"disambiguationData":[TD([makeQuery(id+"F1.opExtrude","SWEPT_FACE",FACE,{"disambiguationData":[OSD([subQ6])]})])],"derivedFrom":makeQuery(id+"F1.opExtrude","CAP_FACE",FACE,{"disambiguationData":[OSD([subQ6,subQ8,subQ9,subQ7,subQ4,subQ3,subQ2,subQ1,subQ0,subQ5,subQ10,subQ11])],"isStart":true})});}
            var sketch = newSketch(context, id + "F16", { "sketchPlane" : qUnion([Q0])});
            skLineSegment(sketch, "E79.0", {"start": v(-70, 90) * mm, "end": v(70, 90) * mm});
            skArc(sketch, "E79.1", {"start": v(-70, 90) * mm, "mid": v(-77.07, 87.07) * mm, "end": v(-80, 80) * mm});
            skLineSegment(sketch, "E79.2", {"start": v(-80, -80) * mm, "end": v(-80, 80) * mm});
            skCircle(sketch, "E79.3", {"center": v(-60, 67.5) * mm, "radius": 4 * mm});
            skArc(sketch, "E79.4", {"start": v(-80, -80) * mm, "mid": v(-77.07, -87.07) * mm, "end": v(-70, -90) * mm});
            skLineSegment(sketch, "E79.5", {"start": v(-70, -90) * mm, "end": v(70, -90) * mm});
            skArc(sketch, "E79.6", {"start": v(70, -90) * mm, "mid": v(77.07, -87.07) * mm, "end": v(80, -80) * mm});
            skLineSegment(sketch, "E79.7", {"start": v(80, -80) * mm, "end": v(80, 80) * mm});
            skArc(sketch, "E79.8", {"start": v(80, 80) * mm, "mid": v(77.07, 87.07) * mm, "end": v(70, 90) * mm});
            skArc(sketch, "E79.9", {"start": v(56.15, 48.18) * mm, "mid": v(0, 67.5) * mm, "end": v(-56.15, 48.18) * mm});
            skCircle(sketch, "E79.10", {"center": v(60, 67.5) * mm, "radius": 4 * mm});
            skCircle(sketch, "E79.11", {"center": v(60, -67.5) * mm, "radius": 4 * mm});
            skCircle(sketch, "E79.12", {"center": v(-60, -67.5) * mm, "radius": 4 * mm});
            skLineSegment(sketch, "E79.13", {"start": v(-60, 40.3) * mm, "end": v(-60, -40.3) * mm});
            skArc(sketch, "E79.14", {"start": v(-56.15, 48.18) * mm, "mid": v(-58.99, 44.68) * mm, "end": v(-60, 40.3) * mm});
            skArc(sketch, "E79.15", {"start": v(60, 40.3) * mm, "mid": v(58.99, 44.68) * mm, "end": v(56.15, 48.18) * mm});
            skLineSegment(sketch, "E79.16", {"start": v(60, 40.3) * mm, "end": v(60, -40.3) * mm});
            skArc(sketch, "E79.17", {"start": v(56.15, -48.18) * mm, "mid": v(58.99, -44.68) * mm, "end": v(60, -40.3) * mm});
            skArc(sketch, "E79.18", {"start": v(-56.15, -48.18) * mm, "mid": v(0, -67.5) * mm, "end": v(56.15, -48.18) * mm});
            skArc(sketch, "E79.19", {"start": v(-60, -40.3) * mm, "mid": v(-58.99, -44.68) * mm, "end": v(-56.15, -48.18) * mm});
            skLineSegment(sketch, "E80", {"start": v(0, 90) * mm, "end": v(0, 120) * mm, "construction": true});
            skLineSegment(sketch, "E81", {"start": v(-15, 108) * mm, "end": v(-33, 90) * mm});
            skLineSegment(sketch, "E82", {"start": v(15, 108) * mm, "end": v(33, 90) * mm});
            skLineSegment(sketch, "E83", {"start": v(-15, 108) * mm, "end": v(-15, 120) * mm});
            skLineSegment(sketch, "E84", {"start": v(15, 108) * mm, "end": v(15, 120) * mm});
            skCircle(sketch, "E85", {"center": v(0, 120) * mm, "radius": 6 * mm});
            skArc(sketch, "E86", {"start": v(15, 120) * mm, "mid": v(0, 135) * mm, "end": v(-15, 120) * mm});
            skLineSegment(sketch, "E87", {"start": v(-80, 0) * mm, "end": v(80, 0) * mm, "construction": true});
            skLineSegment(sketch, "E88.MirrorCS", {"start": v(15, -108) * mm, "end": v(15, -120) * mm});
            skLineSegment(sketch, "E89.MirrorCS", {"start": v(15, -108) * mm, "end": v(33, -90) * mm});
            skArc(sketch, "E90.MirrorCS", {"start": v(15, -120) * mm, "mid": v(0, -135) * mm, "end": v(-15, -120) * mm});
            skArc(sketch, "E91.MirrorCS", {"start": v(-70, -90) * mm, "mid": v(-77.07, -87.07) * mm, "end": v(-80, -80) * mm});
            skCircle(sketch, "E92.MirrorC", {"center": v(0, -120) * mm, "radius": 6 * mm});
            skLineSegment(sketch, "E93.MirrorCS", {"start": v(-15, -108) * mm, "end": v(-15, -120) * mm});
            skLineSegment(sketch, "E94.MirrorCS", {"start": v(-15, -108) * mm, "end": v(-33, -90) * mm});
            skLineSegment(sketch, "E95.MirrorCS", {"start": v(0, -90) * mm, "end": v(0, -120) * mm, "construction": true});
            skArc(sketch, "E96.MirrorCS", {"start": v(80, -80) * mm, "mid": v(77.07, -87.07) * mm, "end": v(70, -90) * mm});
            skSolve(sketch);
        }
        {
            var Q0;
            Q0=makeQuery(id+"F16.imprint","IMPRINT",FACE,{"disambiguationData":[TD([[makeQuery(id+"F16.imprint","IMPRINT",EDGE,{"derivedFrom":sQuery(id+"F16.wireOp",EDGE,"E88.MirrorCS")}),-1.0]])]});
            var Q1;
            {var subQ3=sQuery(id+"F16.wireOp",EDGE,"E79.1");Q1=makeQuery(id+"F16.imprint","IMPRINT",FACE,{"disambiguationData":[TD([[makeQuery(id+"F16.imprint","IMPRINT",EDGE,{"derivedFrom":subQ3}),1.0]])]});}
            var Q2;
            {var subQ1=sQuery(id+"F16.wireOp",EDGE,"E81");Q2=makeQuery(id+"F16.imprint","IMPRINT",FACE,{"disambiguationData":[TD([[makeQuery(id+"F16.imprint","IMPRINT",EDGE,{"derivedFrom":subQ1}),1.0]])]});}
            var Q3;
            Q3=makeQuery(id+"F2.opExtrude","CAP_FACE",FACE,{"disambiguationData":[OSD([sQuery(id+"F0.wireOp",EDGE,"E12"),sQuery(id+"F0.wireOp",EDGE,"E13"),sQuery(id+"F0.wireOp",EDGE,"E14"),sQuery(id+"F0.wireOp",EDGE,"E15"),sQuery(id+"F0.wireOp",EDGE,"E17.filletArc"),sQuery(id+"F0.wireOp",EDGE,"E18.filletArc"),sQuery(id+"F0.wireOp",EDGE,"E19.filletArc"),sQuery(id+"F0.wireOp",EDGE,"E20.filletArc"),sQuery(id+"F0.wireOp",EDGE,"E25.0"),sQuery(id+"F0.wireOp",EDGE,"E25.1"),sQuery(id+"F0.wireOp",EDGE,"E25.2"),sQuery(id+"F0.wireOp",EDGE,"E25.3"),sQuery(id+"F0.wireOp",EDGE,"E25.4"),sQuery(id+"F0.wireOp",EDGE,"E25.5"),sQuery(id+"F0.wireOp",EDGE,"E25.6"),sQuery(id+"F0.wireOp",EDGE,"E25.7")])],"isStart":false});
            extrude(context, id + "F17", {"entities" : qUnion([Q0, Q1, Q2]), "endBound" : BoundingType.UP_TO_SURFACE, "endBoundEntityFace" : qUnion([Q3]), "depth" : 25 * mm});
        }
    });
